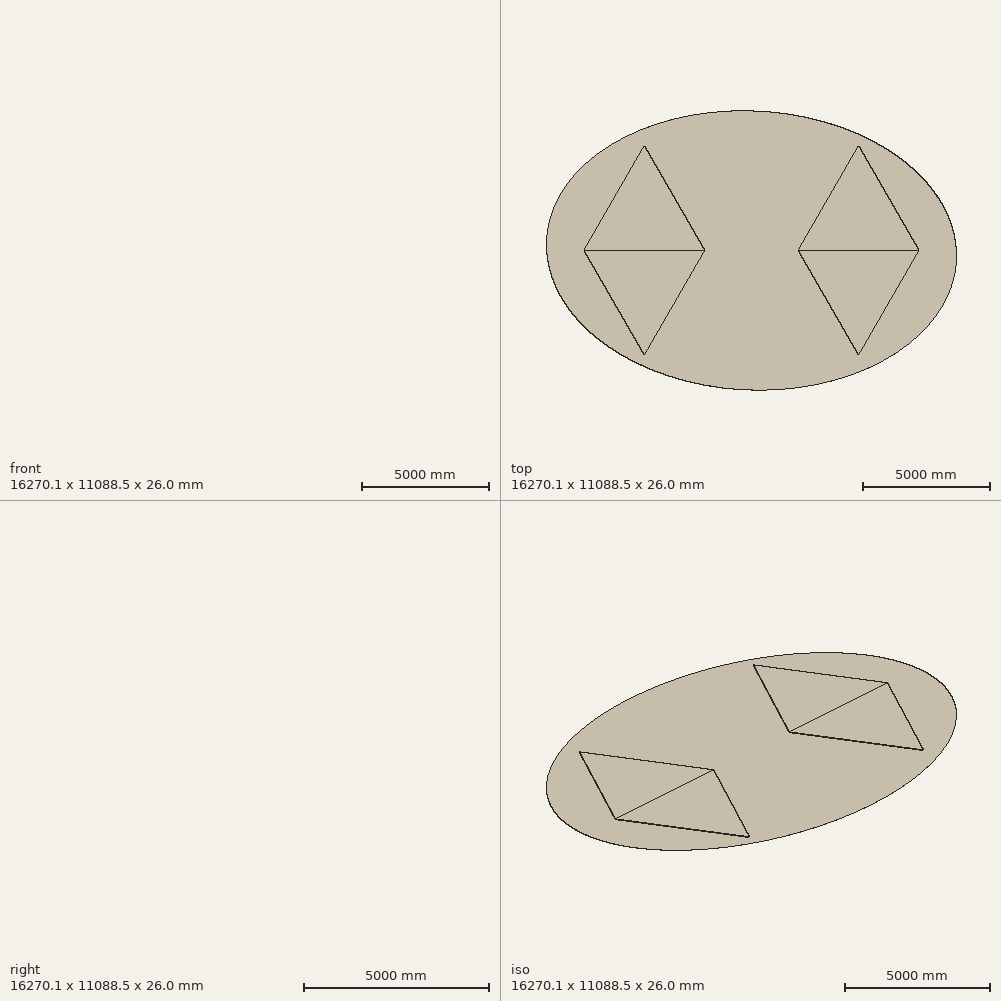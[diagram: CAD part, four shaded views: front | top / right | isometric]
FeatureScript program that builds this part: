
annotation { "Feature Type Name" : "Feature", "Feature Type Description" : "" }
export const myFeature = defineFeature(function(context is Context, id is Id, definition is map)
    precondition{}
    {
        {
            var Q0;
            Q0=qCreatedBy(makeId("Top.planeOp"),FACE);
            var sketch = newSketch(context, id + "F0", { "sketchPlane" : qUnion([Q0])});
            skLineSegment(sketch, "E0", {"start": v(0, 0) * mm, "end": v(-1850, 0) * mm});
            skLineSegment(sketch, "E1", {"start": v(-1850, 0) * mm, "end": v(-6650, 0) * mm});
            skLineSegment(sketch, "E2", {"start": v(0, 0) * mm, "end": v(1850, 0) * mm});
            skLineSegment(sketch, "E3", {"start": v(1850, 0) * mm, "end": v(6650, 0) * mm});
            skLineSegment(sketch, "E4", {"start": v(1850, 0) * mm, "end": v(4250, 4156.92) * mm});
            skLineSegment(sketch, "E5", {"start": v(4250, 4156.92) * mm, "end": v(6650, 0) * mm});
            skLineSegment(sketch, "E6", {"start": v(6650, 0) * mm, "end": v(4250, -4156.92) * mm});
            skLineSegment(sketch, "E7", {"start": v(4250, -4156.92) * mm, "end": v(1850, 0) * mm});
            skLineSegment(sketch, "E8", {"start": v(-6650, 0) * mm, "end": v(-4250, 4156.92) * mm});
            skLineSegment(sketch, "E9", {"start": v(-4250, 4156.92) * mm, "end": v(-1850, 0) * mm});
            skLineSegment(sketch, "E10", {"start": v(-1850, 0) * mm, "end": v(-4250, -4156.92) * mm});
            skLineSegment(sketch, "E11", {"start": v(-4250, -4156.92) * mm, "end": v(-6650, 0) * mm});
            skPoint(sketch, "E12", {"position": v(-4250, 4156.92) * mm});
            skPoint(sketch, "E13", {"position": v(-6650, 0) * mm});
            skPoint(sketch, "E14", {"position": v(-4250, -4156.92) * mm});
            skPoint(sketch, "E15", {"position": v(4250, -4156.92) * mm});
            skPoint(sketch, "E16", {"position": v(6650, 0) * mm});
            skPoint(sketch, "E17", {"position": v(4250, 4156.92) * mm});
            skSolve(sketch);
        }
        {
            var Q0;
            Q0=qCreatedBy(makeId("Top.planeOp"),FACE);
            var sketch = newSketch(context, id + "F1", { "sketchPlane" : qUnion([Q0])});
            skEllipse(sketch, "E18", {"center": v(0, 0) * mm, "majorRadius": 8140.4 * mm, "minorRadius": 5536.36 * mm, "majorAxis": v(1, -0.05)});
            skSolve(sketch);
        }
        {
            var Q0;
            Q0=makeQuery(id+"F1.imprint","IMPRINT",FACE,{"disambiguationData":[TD([[makeQuery(id+"F1.imprint","IMPRINT",EDGE,{"derivedFrom":sQuery(id+"F1.wireOp",EDGE,"E18")}),1.0]])]});
            var Q1;
            Q1=makeQuery(id+"F1.imprint","IMPRINT",FACE,{"disambiguationData":[TD([[makeQuery(id+"F1.imprint","IMPRINT",EDGE,{"derivedFrom":sQuery(id+"F1.wireOp",EDGE,"E18")}),1.0]])]});
            extrude(context, id + "F2", {"entities" : qUnion([Q0, Q1]), "oppositeDirection" : true, "depth" : 1 * mm, "offsetDistance" : 25 * mm});
        }
        {
            var Q0;
            {var subQ3=sQuery(id+"F0.wireOp",EDGE,"E8");Q0=makeQuery(id+"F0.imprint","IMPRINT",FACE,{"disambiguationData":[TD([[makeQuery(id+"F0.imprint","IMPRINT",EDGE,{"derivedFrom":subQ3}),-1.0]])]});}
            var Q1;
            {var subQ3=sQuery(id+"F0.wireOp",EDGE,"E6");Q1=makeQuery(id+"F0.imprint","IMPRINT",FACE,{"disambiguationData":[TD([[makeQuery(id+"F0.imprint","IMPRINT",EDGE,{"derivedFrom":subQ3}),-1.0]])]});}
            extrude(context, id + "F3", {"entities" : qUnion([Q0, Q1]), "operationType" : NewBodyOperationType.ADD, "depth" : 25 * mm, "offsetDistance" : 25 * mm});
        }
        {
            var Q0;
            {var subQ3=sQuery(id+"F0.wireOp",EDGE,"E11");Q0=makeQuery(id+"F0.imprint","IMPRINT",FACE,{"disambiguationData":[TD([[makeQuery(id+"F0.imprint","IMPRINT",EDGE,{"derivedFrom":subQ3}),-1.0]])]});}
            var Q1;
            {var subQ3=sQuery(id+"F0.wireOp",EDGE,"E5");Q1=makeQuery(id+"F0.imprint","IMPRINT",FACE,{"disambiguationData":[TD([[makeQuery(id+"F0.imprint","IMPRINT",EDGE,{"derivedFrom":subQ3}),-1.0]])]});}
            extrude(context, id + "F4", {"entities" : qUnion([Q0, Q1]), "depth" : 25 * mm, "offsetDistance" : 25 * mm});
        }
    });
